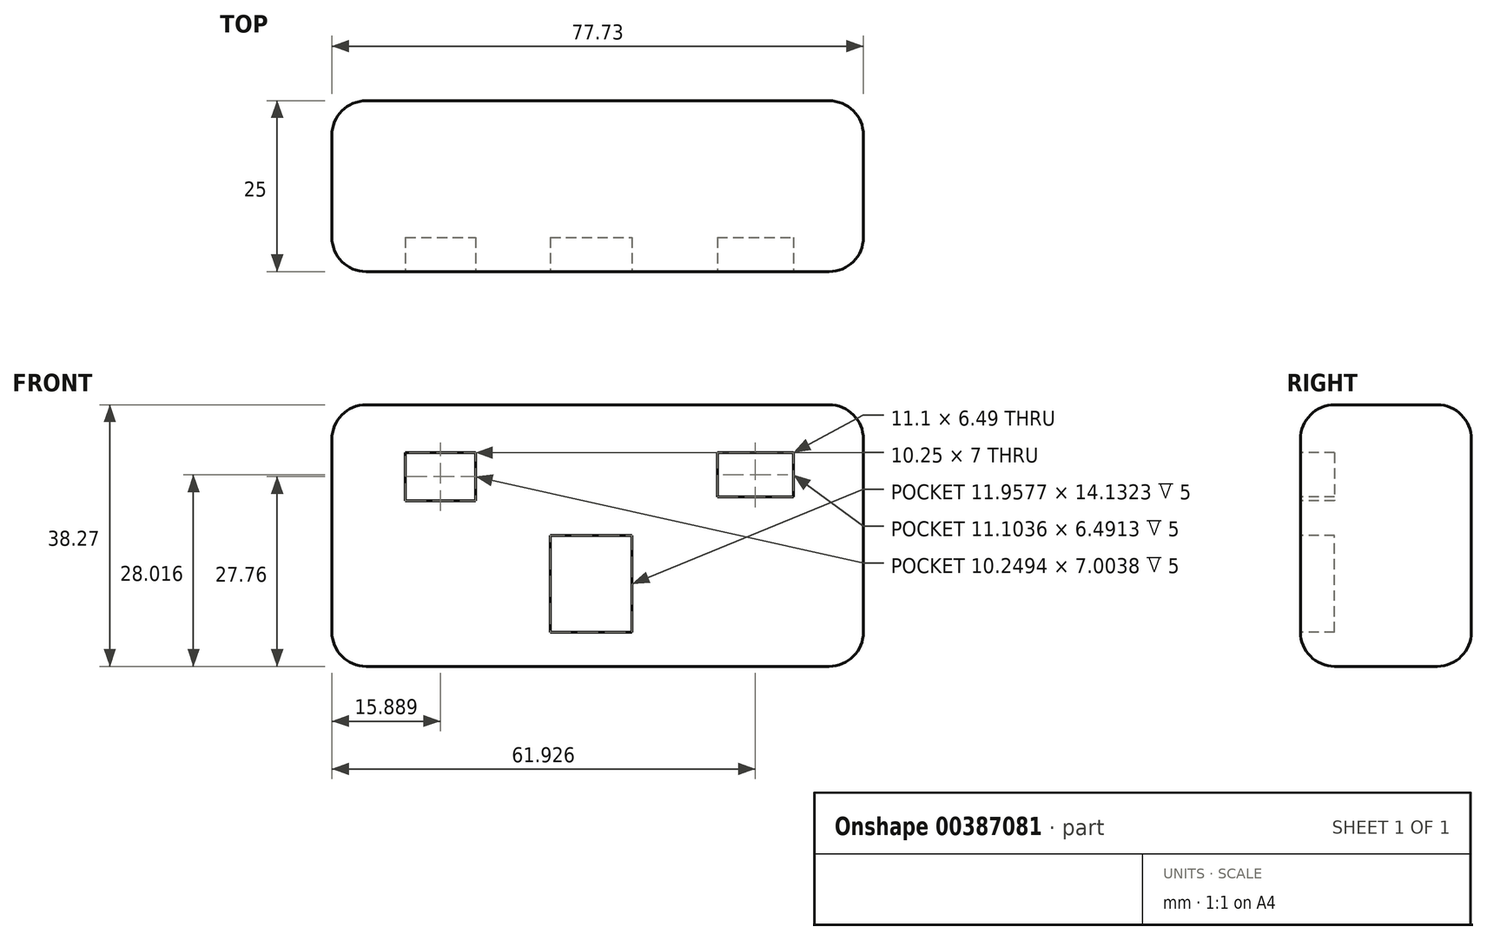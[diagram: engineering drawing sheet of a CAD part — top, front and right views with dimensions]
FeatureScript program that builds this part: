
annotation { "Feature Type Name" : "Feature", "Feature Type Description" : "" }
export const myFeature = defineFeature(function(context is Context, id is Id, definition is map)
    precondition{}
    {
        {
            var Q0;
            Q0=qCreatedBy(makeId("Front.planeOp"),FACE);
            var sketch = newSketch(context, id + "F0", { "sketchPlane" : qUnion([Q0])});
            skLineSegment(sketch, "E0.bottom", {"start": v(-52.36, 5.64) * mm, "end": v(25.37, 5.64) * mm});
            skLineSegment(sketch, "E0.top", {"start": v(-52.36, -32.63) * mm, "end": v(25.37, -32.63) * mm});
            skLineSegment(sketch, "E0.left", {"start": v(-52.36, 5.64) * mm, "end": v(-52.36, -32.63) * mm});
            skLineSegment(sketch, "E0.right", {"start": v(25.37, 5.64) * mm, "end": v(25.37, -32.63) * mm});
            skSolve(sketch);
        }
        {
            var Q0;
            Q0 = qSketchRegion(id + "F0", true);
            extrude(context, id + "F1", {"entities" : qUnion([Q0]), "depth" : 25 * mm});
        }
        {
            var Q0;
            Q0=makeQuery(id+"F1.opExtrude","CAP_EDGE",EDGE,{"disambiguationData":[OSD([sQuery(id+"F0.wireOp",EDGE,"E0.left")])],"isStart":false});
            var Q1;
            Q1=makeQuery(id+"F1.opExtrude","SWEPT_FACE",FACE,{"disambiguationData":[OSD([sQuery(id+"F0.wireOp",EDGE,"E0.bottom")])]});
            var Q2;
            Q2=makeQuery(id+"F1.opExtrude","CAP_FACE",FACE,{"disambiguationData":[OSD([sQuery(id+"F0.wireOp",EDGE,"E0.bottom"),sQuery(id+"F0.wireOp",EDGE,"E0.top"),sQuery(id+"F0.wireOp",EDGE,"E0.left"),sQuery(id+"F0.wireOp",EDGE,"E0.right")])],"isStart":false});
            var Q3;
            Q3=makeQuery(id+"F1.opExtrude","SWEPT_FACE",FACE,{"disambiguationData":[OSD([sQuery(id+"F0.wireOp",EDGE,"E0.right")])]});
            var Q4;
            Q4=makeQuery(id+"F1.opExtrude","CAP_FACE",FACE,{"disambiguationData":[OSD([sQuery(id+"F0.wireOp",EDGE,"E0.bottom"),sQuery(id+"F0.wireOp",EDGE,"E0.top"),sQuery(id+"F0.wireOp",EDGE,"E0.left"),sQuery(id+"F0.wireOp",EDGE,"E0.right")])],"isStart":true});
            var Q5;
            Q5=makeQuery(id+"F1.opExtrude","SWEPT_FACE",FACE,{"disambiguationData":[OSD([sQuery(id+"F0.wireOp",EDGE,"E0.top")])]});
            var Q6;
            Q6=makeQuery(id+"F1.opExtrude","SWEPT_FACE",FACE,{"disambiguationData":[OSD([sQuery(id+"F0.wireOp",EDGE,"E0.left")])]});
            fillet(context, id + "F2", {"entities" : qUnion([Q0, Q1, Q2, Q3, Q4, Q5, Q6]), "radius" : 5 * mm, "tangentPropagation" : true, "allowEdgeOverflow" : false});
        }
        {
            var Q0;
            Q0=makeQuery(id+"F1.opExtrude","CAP_FACE",FACE,{"disambiguationData":[OSD([sQuery(id+"F0.wireOp",EDGE,"E0.bottom"),sQuery(id+"F0.wireOp",EDGE,"E0.top"),sQuery(id+"F0.wireOp",EDGE,"E0.left"),sQuery(id+"F0.wireOp",EDGE,"E0.right")])],"isStart":false});
            var sketch = newSketch(context, id + "F3", { "sketchPlane" : qUnion([Q0])});
            skLineSegment(sketch, "E1.bottom", {"start": v(-41.6, -1.37) * mm, "end": v(-31.35, -1.37) * mm});
            skLineSegment(sketch, "E1.top", {"start": v(-41.6, -8.37) * mm, "end": v(-31.35, -8.37) * mm});
            skLineSegment(sketch, "E1.left", {"start": v(-41.6, -1.37) * mm, "end": v(-41.6, -8.37) * mm});
            skLineSegment(sketch, "E1.right", {"start": v(-31.35, -1.37) * mm, "end": v(-31.35, -8.37) * mm});
            skLineSegment(sketch, "E2.bottom", {"start": v(4.01, -1.37) * mm, "end": v(15.12, -1.37) * mm});
            skLineSegment(sketch, "E2.top", {"start": v(4.01, -7.86) * mm, "end": v(15.12, -7.86) * mm});
            skLineSegment(sketch, "E2.left", {"start": v(4.01, -1.37) * mm, "end": v(4.01, -7.86) * mm});
            skLineSegment(sketch, "E2.right", {"start": v(15.12, -1.37) * mm, "end": v(15.12, -7.86) * mm});
            skLineSegment(sketch, "E3.bottom", {"start": v(-20.41, -27.63) * mm, "end": v(-8.46, -27.63) * mm});
            skLineSegment(sketch, "E3.top", {"start": v(-20.41, -13.5) * mm, "end": v(-8.46, -13.5) * mm});
            skLineSegment(sketch, "E3.left", {"start": v(-20.41, -27.63) * mm, "end": v(-20.41, -13.5) * mm});
            skLineSegment(sketch, "E3.right", {"start": v(-8.46, -27.63) * mm, "end": v(-8.46, -13.5) * mm});
            skSolve(sketch);
        }
        {
            var Q0;
            Q0 = qSketchRegion(id + "F3", true);
            extrude(context, id + "F4", {"entities" : qUnion([Q0]), "operationType" : NewBodyOperationType.REMOVE, "oppositeDirection" : true, "depth" : 5 * mm});
        }
    });
